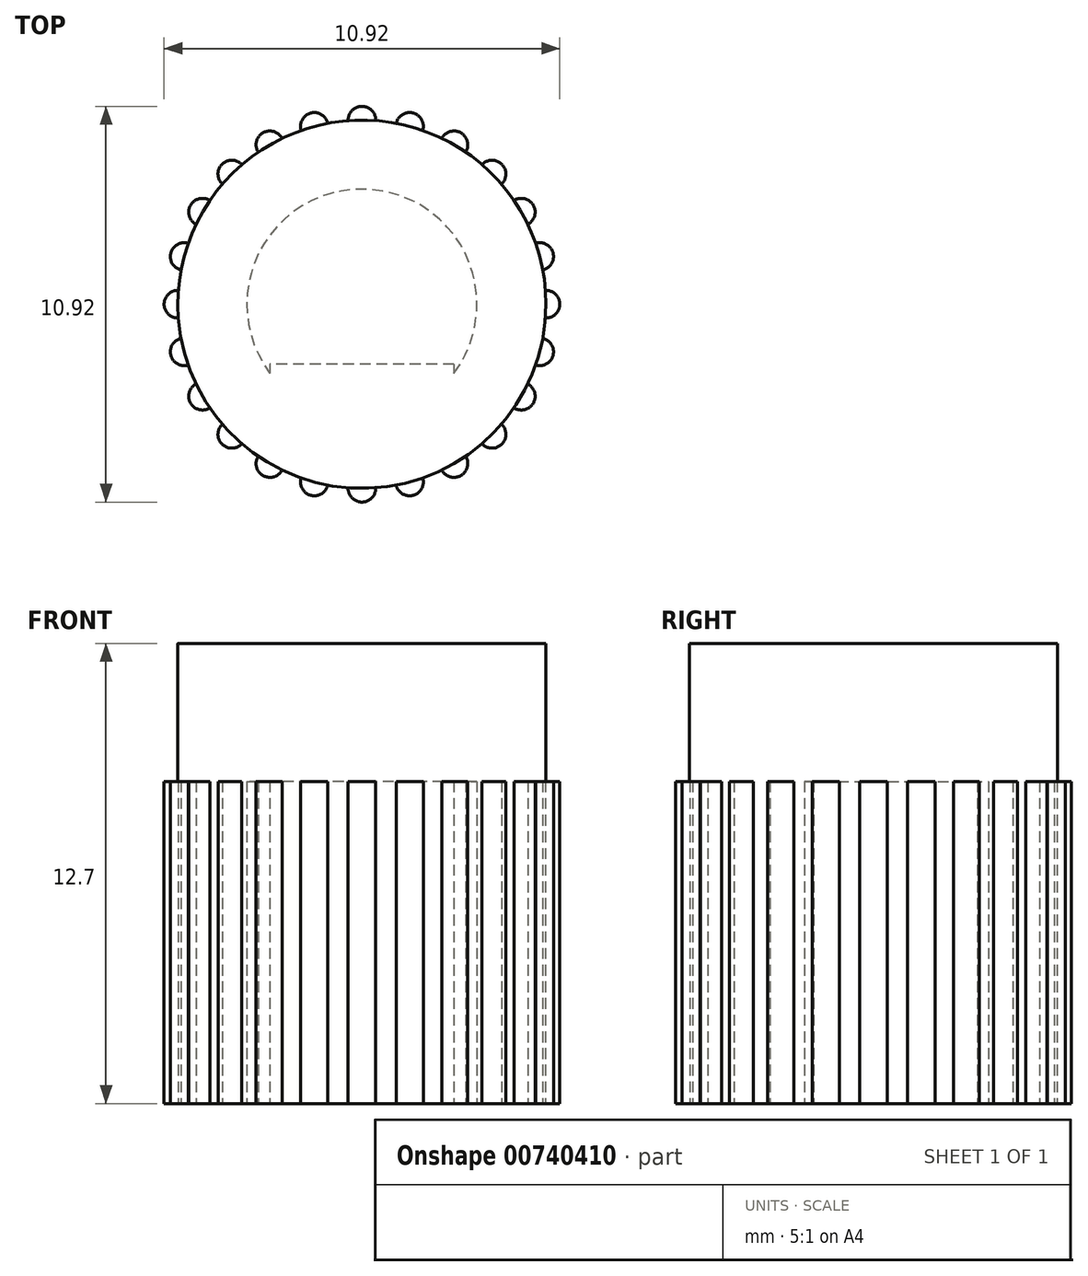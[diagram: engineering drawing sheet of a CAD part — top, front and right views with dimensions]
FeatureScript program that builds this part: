
annotation { "Feature Type Name" : "Feature", "Feature Type Description" : "" }
export const myFeature = defineFeature(function(context is Context, id is Id, definition is map)
    precondition{}
    {
        {
            var Q0;
            Q0=qCreatedBy(makeId("Top.planeOp"),FACE);
            var sketch = newSketch(context, id + "F0", { "sketchPlane" : qUnion([Q0])});
            skCircle(sketch, "E0", {"center": v(0, 0) * mm, "radius": 3.18 * mm});
            skCircle(sketch, "E1", {"center": v(0, 0) * mm, "radius": 5.08 * mm});
            skCircle(sketch, "E2", {"center": v(0, 5.08) * mm, "radius": 0.38 * mm});
            skCircle(sketch, "E3.1.0", {"center": v(-1.31, 4.9) * mm, "radius": 0.38 * mm});
            skCircle(sketch, "E3.2.0", {"center": v(-2.54, 4.4) * mm, "radius": 0.38 * mm});
            skCircle(sketch, "E3.3.0", {"center": v(-3.6, 3.6) * mm, "radius": 0.38 * mm});
            skCircle(sketch, "E3.4.0", {"center": v(-4.4, 2.54) * mm, "radius": 0.38 * mm});
            skCircle(sketch, "E3.5.0", {"center": v(-4.9, 1.31) * mm, "radius": 0.38 * mm});
            skCircle(sketch, "E3.6.0", {"center": v(-5.08, 0) * mm, "radius": 0.38 * mm});
            skCircle(sketch, "E3.7.0", {"center": v(-4.9, -1.31) * mm, "radius": 0.38 * mm});
            skCircle(sketch, "E3.8.0", {"center": v(-4.4, -2.54) * mm, "radius": 0.38 * mm});
            skCircle(sketch, "E3.9.0", {"center": v(-3.6, -3.6) * mm, "radius": 0.38 * mm});
            skCircle(sketch, "E3.10.0", {"center": v(-2.54, -4.4) * mm, "radius": 0.38 * mm});
            skCircle(sketch, "E3.11.0", {"center": v(-1.31, -4.9) * mm, "radius": 0.38 * mm});
            skCircle(sketch, "E3.12.0", {"center": v(0, -5.08) * mm, "radius": 0.38 * mm});
            skCircle(sketch, "E3.13.0", {"center": v(1.31, -4.9) * mm, "radius": 0.38 * mm});
            skCircle(sketch, "E3.14.0", {"center": v(2.54, -4.4) * mm, "radius": 0.38 * mm});
            skCircle(sketch, "E3.15.0", {"center": v(3.6, -3.6) * mm, "radius": 0.38 * mm});
            skCircle(sketch, "E3.16.0", {"center": v(4.4, -2.54) * mm, "radius": 0.38 * mm});
            skCircle(sketch, "E3.17.0", {"center": v(4.9, -1.31) * mm, "radius": 0.38 * mm});
            skCircle(sketch, "E3.18.0", {"center": v(5.08, 0) * mm, "radius": 0.38 * mm});
            skCircle(sketch, "E3.19.0", {"center": v(4.9, 1.31) * mm, "radius": 0.38 * mm});
            skCircle(sketch, "E3.20.0", {"center": v(4.4, 2.54) * mm, "radius": 0.38 * mm});
            skCircle(sketch, "E3.21.0", {"center": v(3.6, 3.6) * mm, "radius": 0.38 * mm});
            skCircle(sketch, "E3.22.0", {"center": v(2.54, 4.4) * mm, "radius": 0.38 * mm});
            skCircle(sketch, "E3.23.0", {"center": v(1.31, 4.9) * mm, "radius": 0.38 * mm});
            skSolve(sketch);
        }
        {
            var Q0;
            Q0=qCreatedBy(makeId("Top.planeOp"),FACE);
            var sketch = newSketch(context, id + "F1", { "sketchPlane" : qUnion([Q0])});
            skLineSegment(sketch, "E4.bottom", {"start": v(2.54, -1.65) * mm, "end": v(-2.54, -1.65) * mm});
            skLineSegment(sketch, "E4.top", {"start": v(2.54, -3.68) * mm, "end": v(-2.54, -3.68) * mm});
            skLineSegment(sketch, "E4.left", {"start": v(2.54, -1.65) * mm, "end": v(2.54, -3.68) * mm});
            skLineSegment(sketch, "E4.right", {"start": v(-2.54, -1.65) * mm, "end": v(-2.54, -3.68) * mm});
            skPoint(sketch, "E4.middle", {"position": v(0, -2.67) * mm});
            skSolve(sketch);
        }
        {
            var Q0;
            Q0 = qSketchRegion(id + "F0", true);
            extrude(context, id + "F2", {"entities" : qUnion([Q0]), "depth" : 8.9 * mm, "offsetDistance" : 25.4 * mm});
        }
        {
            var Q0;
            Q0 = qSketchRegion(id + "F1", true);
            extrude(context, id + "F3", {"entities" : qUnion([Q0]), "operationType" : NewBodyOperationType.ADD, "depth" : 8.9 * mm, "offsetDistance" : 25.4 * mm});
        }
        {
            var Q0;
            Q0=qCreatedBy(makeId("Top.planeOp"),FACE);
            cPlane(context, id + "F4", {"entities" : qUnion([Q0]), "cplaneType" : CPlaneType.OFFSET, "offset" : 8.9 * mm, "width" : 152.4 * mm, "height" : 152.4 * mm});
        }
        {
            var Q0;
            Q0=qCreatedBy(id+"F4.planeOp",FACE);
            var sketch = newSketch(context, id + "F5", { "sketchPlane" : qUnion([Q0])});
            skCircle(sketch, "E5", {"center": v(0, 0) * mm, "radius": 5.08 * mm});
            skSolve(sketch);
        }
        {
            var Q0;
            Q0 = qSketchRegion(id + "F5", true);
            extrude(context, id + "F6", {"entities" : qUnion([Q0]), "operationType" : NewBodyOperationType.ADD, "depth" : 3.8 * mm, "offsetDistance" : 25.4 * mm});
        }
    });
